# Revit family: Receptacle - BA
name_source: partatom
category: Electrical Fixtures
revit_build: Autodesk Revit 2018 (Build: 20181011_1500(x64)
units: mm (PartAtom-declared; Revit-internal decimal feet)

## family parameters
Cut with Voids When Loaded = Yes
Host = Face
Maintain Annotation Orientation = Yes
Part Type = Normal
Room Calculation Point = No
Round Connector Dimension = Use Diameter
Shared = No

## types (7) — shared parameters
Box Height = 0' - 3"
Box Width = 0' - 1 1/2"
Faceplate Height = 0' - 4 1/2"
Faceplate Width = 0' - 2 3/4"

## per-type parameters (varying)
| type | Default Elevation | Duplex | GFCI | Quad | Simplex | Special | Switched |
| Duplex | 1' - 6" | Yes | No | No | No | No | No |
| Duplex GFCI | 3' - 6" | Yes | Yes | No | No | No | No |
| Simplex | 1' - 6" | No | No | No | Yes | No | No |
| Quad | 1' - 6" | Yes | No | Yes | No | No | No |
| Quad GFCI | 3' - 6" | Yes | Yes | Yes | No | No | No |
| Special | 1' - 6" | No | No | No | No | Yes | No |
| Switched | 1' - 6" | Yes | No | No | No | No | Yes |

## geometry (parser evidence)
native form markers: Sweep x2
no freeform markers — native parametric forms only
